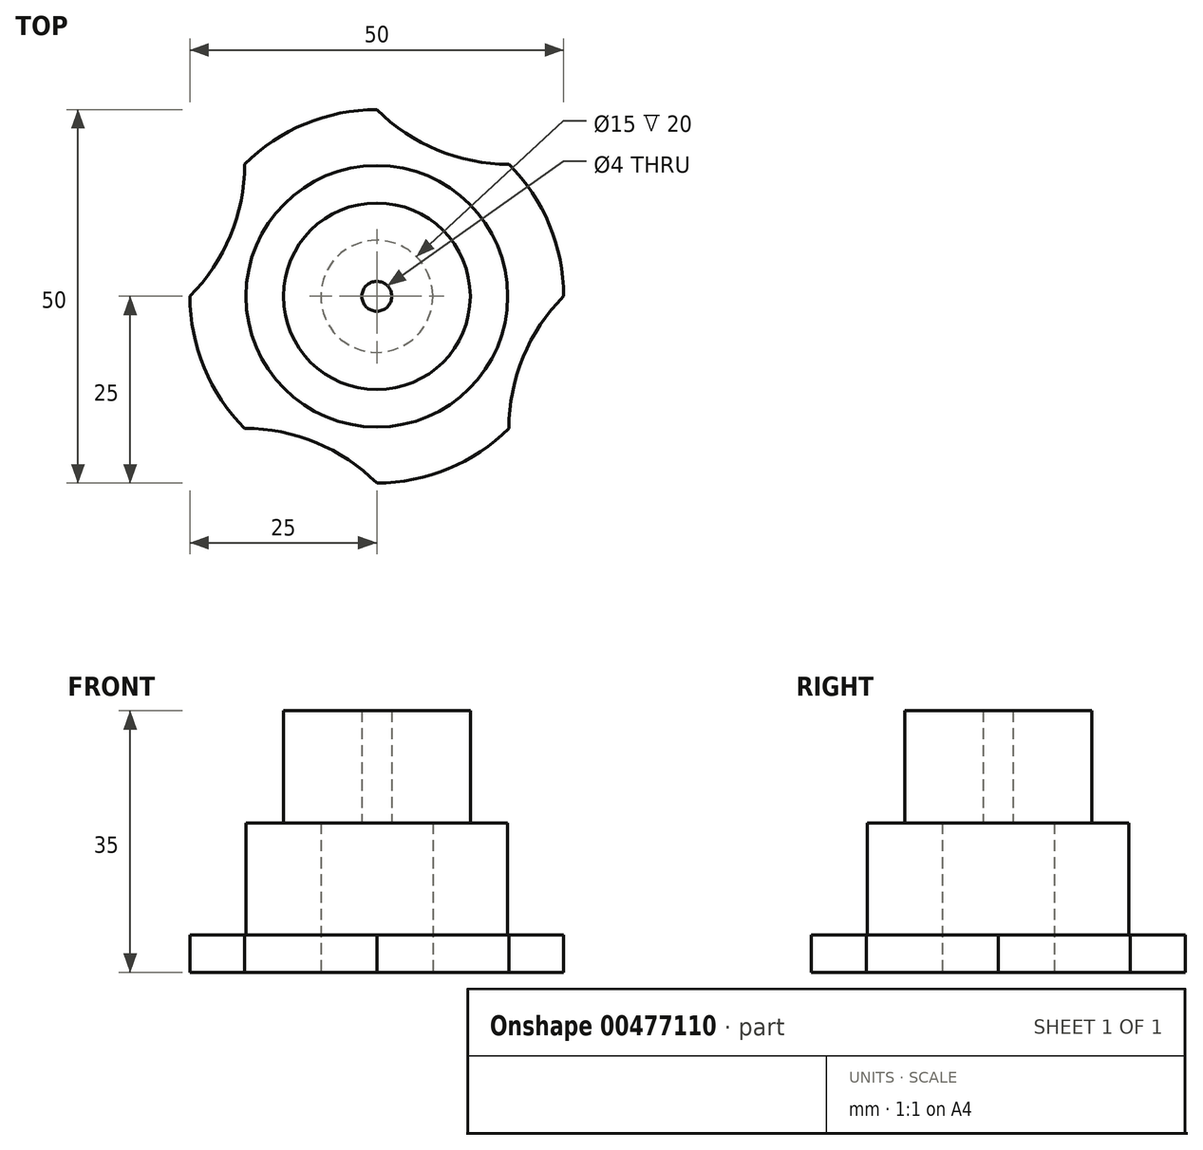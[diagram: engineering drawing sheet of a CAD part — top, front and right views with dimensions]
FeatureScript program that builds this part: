
annotation { "Feature Type Name" : "Feature", "Feature Type Description" : "" }
export const myFeature = defineFeature(function(context is Context, id is Id, definition is map)
    precondition{}
    {
        {
            var Q0;
            Q0=qCreatedBy(makeId("Top.planeOp"),FACE);
            var sketch = newSketch(context, id + "F0", { "sketchPlane" : qUnion([Q0])});
            skCircle(sketch, "E0", {"center": v(0, 0) * mm, "radius": 7.5 * mm});
            skArc(sketch, "E1", {"start": v(-25, 0) * mm, "mid": v(-23.1, -9.57) * mm, "end": v(-17.68, -17.68) * mm});
            skLineSegment(sketch, "E2", {"start": v(0, 0) * mm, "end": v(-52.42, 0) * mm, "construction": true});
            skLineSegment(sketch, "E3.1.0", {"start": v(0, 0) * mm, "end": v(-48.43, -20.06) * mm, "construction": true});
            skLineSegment(sketch, "E3.2.0", {"start": v(0, 0) * mm, "end": v(-37.07, -37.07) * mm, "construction": true});
            skLineSegment(sketch, "E3.3.0", {"start": v(0, 0) * mm, "end": v(-20.06, -48.43) * mm, "construction": true});
            skLineSegment(sketch, "E3.4.0", {"start": v(0, 0) * mm, "end": v(0, -52.42) * mm, "construction": true});
            skLineSegment(sketch, "E3.5.0", {"start": v(0, 0) * mm, "end": v(20.06, -48.43) * mm, "construction": true});
            skLineSegment(sketch, "E3.6.0", {"start": v(0, 0) * mm, "end": v(37.07, -37.07) * mm, "construction": true});
            skLineSegment(sketch, "E3.7.0", {"start": v(0, 0) * mm, "end": v(48.43, -20.06) * mm, "construction": true});
            skLineSegment(sketch, "E3.8.0", {"start": v(0, 0) * mm, "end": v(52.42, 0) * mm, "construction": true});
            skLineSegment(sketch, "E3.9.0", {"start": v(0, 0) * mm, "end": v(48.43, 20.06) * mm, "construction": true});
            skLineSegment(sketch, "E3.10.0", {"start": v(0, 0) * mm, "end": v(37.07, 37.07) * mm, "construction": true});
            skLineSegment(sketch, "E3.11.0", {"start": v(0, 0) * mm, "end": v(20.06, 48.43) * mm, "construction": true});
            skLineSegment(sketch, "E3.12.0", {"start": v(0, 0) * mm, "end": v(0, 52.42) * mm, "construction": true});
            skLineSegment(sketch, "E3.13.0", {"start": v(0, 0) * mm, "end": v(-20.06, 48.43) * mm, "construction": true});
            skLineSegment(sketch, "E3.14.0", {"start": v(0, 0) * mm, "end": v(-37.07, 37.07) * mm, "construction": true});
            skLineSegment(sketch, "E3.15.0", {"start": v(0, 0) * mm, "end": v(-48.43, 20.06) * mm, "construction": true});
            skArc(sketch, "E4", {"start": v(-25, 0) * mm, "mid": v(-19.58, 8.11) * mm, "end": v(-17.68, 17.68) * mm});
            skArc(sketch, "E5.1.0", {"start": v(0, -25) * mm, "mid": v(-8.11, -19.58) * mm, "end": v(-17.68, -17.68) * mm});
            skArc(sketch, "E5.2.0", {"start": v(25, 0) * mm, "mid": v(19.58, -8.11) * mm, "end": v(17.68, -17.68) * mm});
            skArc(sketch, "E5.3.0", {"start": v(0, 25) * mm, "mid": v(8.11, 19.58) * mm, "end": v(17.68, 17.68) * mm});
            skArc(sketch, "E6.trimOffspring", {"start": v(0, 25) * mm, "mid": v(-9.57, 23.1) * mm, "end": v(-17.68, 17.68) * mm});
            skArc(sketch, "E7.trimOffspring", {"start": v(25, 0) * mm, "mid": v(23.1, 9.57) * mm, "end": v(17.68, 17.68) * mm});
            skArc(sketch, "E8.trimOffspring", {"start": v(0, -25) * mm, "mid": v(9.57, -23.1) * mm, "end": v(17.68, -17.68) * mm});
            skSolve(sketch);
        }
        {
            var Q0;
            Q0=makeQuery(id+"F0.imprint","IMPRINT",FACE,{"disambiguationData":[TD([[makeQuery(id+"F0.imprint","IMPRINT",EDGE,{"derivedFrom":sQuery(id+"F0.wireOp",EDGE,"E0")}),-1.0]])]});
            extrude(context, id + "F1", {"entities" : qUnion([Q0]), "depth" : 5 * mm});
        }
        {
            var Q0;
            Q0=makeQuery(id+"F1.opExtrude","CAP_FACE",FACE,{"disambiguationData":[OSD([sQuery(id+"F0.wireOp",EDGE,"E0"),sQuery(id+"F0.wireOp",EDGE,"E1")])],"isStart":false});
            var sketch = newSketch(context, id + "F2", { "sketchPlane" : qUnion([Q0])});
            skCircle(sketch, "E9", {"center": v(0, 0) * mm, "radius": 17.5 * mm});
            skSolve(sketch);
        }
        {
            var Q0;
            Q0=makeQuery(id+"F2.imprint","IMPRINT",FACE,{"disambiguationData":[TD([[makeQuery(id+"F2.imprint","IMPRINT",EDGE,{"derivedFrom":sQuery(id+"F2.wireOp",EDGE,"E9")}),1.0]])]});
            extrude(context, id + "F3", {"entities" : qUnion([Q0]), "operationType" : NewBodyOperationType.ADD, "depth" : 15 * mm});
        }
        {
            var Q0;
            Q0=makeQuery(id+"F3.opExtrude","CAP_FACE",FACE,{"disambiguationData":[OSD([sQuery(id+"F0.wireOp",EDGE,"E0"),sQuery(id+"F2.wireOp",EDGE,"E9")])],"isStart":false});
            var sketch = newSketch(context, id + "F4", { "sketchPlane" : qUnion([Q0])});
            skCircle(sketch, "E10", {"center": v(0, 0) * mm, "radius": 2 * mm});
            skCircle(sketch, "E11", {"center": v(0, 0) * mm, "radius": 12.5 * mm});
            skSolve(sketch);
        }
        {
            var Q0;
            Q0=makeQuery(id+"F4.imprint","IMPRINT",FACE,{"disambiguationData":[TD([[makeQuery(id+"F4.imprint","IMPRINT",EDGE,{"derivedFrom":sQuery(id+"F4.wireOp",EDGE,"E11")}),1.0]])]});
            var Q1;
            Q1=makeQuery(id+"F4.imprint","IMPRINT",FACE,{"disambiguationData":[TD([[makeQuery(id+"F4.imprint","IMPRINT",EDGE,{"derivedFrom":sQuery(id+"F4.wireOp",EDGE,"E10")}),-1.0]])]});
            extrude(context, id + "F5", {"entities" : qUnion([Q0, Q1]), "operationType" : NewBodyOperationType.ADD, "depth" : 15 * mm});
        }
    });
